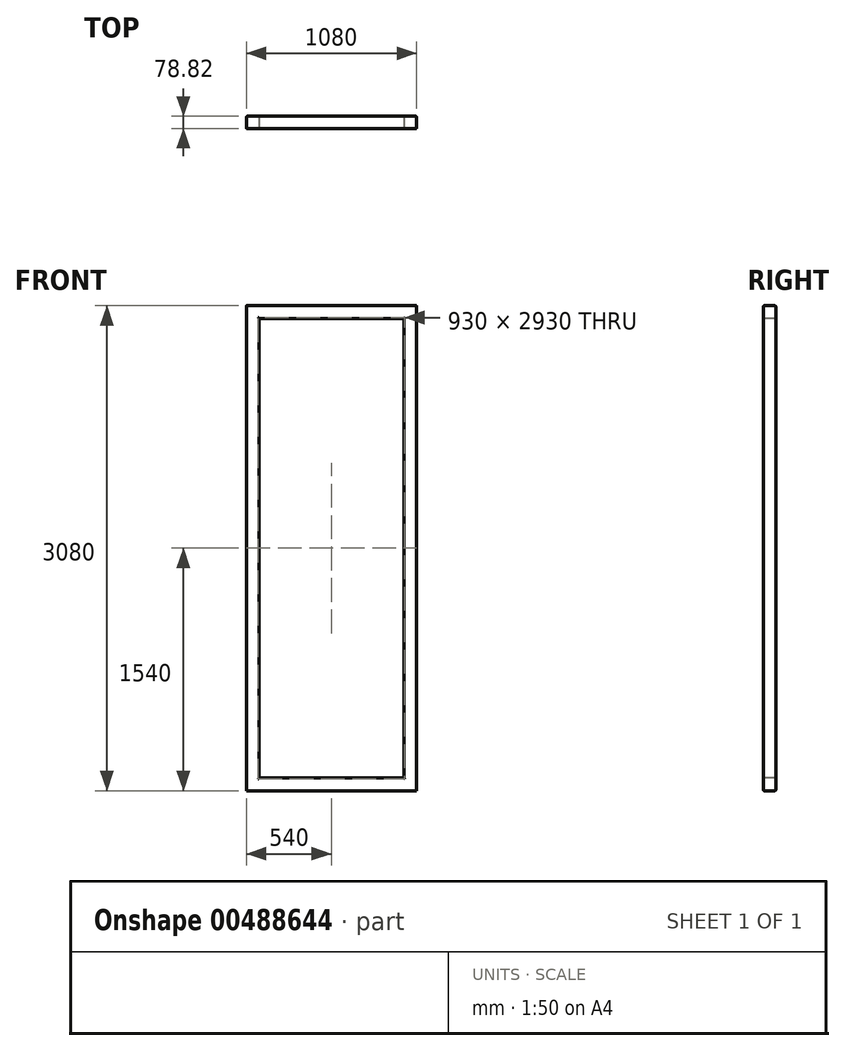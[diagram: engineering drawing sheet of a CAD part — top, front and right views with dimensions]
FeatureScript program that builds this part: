
annotation { "Feature Type Name" : "Feature", "Feature Type Description" : "" }
export const myFeature = defineFeature(function(context is Context, id is Id, definition is map)
    precondition{}
    {
        {
            var Q0;
            Q0=qCreatedBy(makeId("Top.planeOp"),FACE);
            var sketch = newSketch(context, id + "F0", { "sketchPlane" : qUnion([Q0])});
            skLineSegment(sketch, "E0.bottom", {"start": v(35, -39.4) * mm, "end": v(-35, -39.4) * mm});
            skLineSegment(sketch, "E0.top", {"start": v(35, 39.4) * mm, "end": v(-35, 39.4) * mm});
            skLineSegment(sketch, "E0.left", {"start": v(40, -34.4) * mm, "end": v(40, 34.4) * mm});
            skLineSegment(sketch, "E0.right", {"start": v(-40, -34.4) * mm, "end": v(-40, 34.4) * mm});
            skPoint(sketch, "E0.middle", {"position": v(0, 0) * mm});
            skPoint(sketch, "E1.visualSharp", {"position": v(-40, -39.4) * mm});
            skArc(sketch, "E1.filletArc", {"start": v(-40, -34.4) * mm, "mid": v(-38.54, -37.94) * mm, "end": v(-35, -39.4) * mm});
            skPoint(sketch, "E2.visualSharp", {"position": v(-40, 39.4) * mm});
            skArc(sketch, "E2.filletArc", {"start": v(-35, 39.4) * mm, "mid": v(-38.54, 37.94) * mm, "end": v(-40, 34.4) * mm});
            skPoint(sketch, "E3.visualSharp", {"position": v(40, 39.4) * mm});
            skArc(sketch, "E3.filletArc", {"start": v(40, 34.4) * mm, "mid": v(38.54, 37.94) * mm, "end": v(35, 39.4) * mm});
            skPoint(sketch, "E4.visualSharp", {"position": v(40, -39.4) * mm});
            skArc(sketch, "E4.filletArc", {"start": v(35, -39.4) * mm, "mid": v(38.54, -37.94) * mm, "end": v(40, -34.4) * mm});
            skSolve(sketch);
        }
        {
            var Q0;
            Q0=qCreatedBy(makeId("Front.planeOp"),FACE);
            var sketch = newSketch(context, id + "F1", { "sketchPlane" : qUnion([Q0])});
            skLineSegment(sketch, "E5", {"start": v(0, 0) * mm, "end": v(0, 3000) * mm});
            skLineSegment(sketch, "E6", {"start": v(0, 3000) * mm, "end": v(1000, 3000) * mm});
            skLineSegment(sketch, "E7", {"start": v(1000, 3000) * mm, "end": v(1000, 0) * mm});
            skLineSegment(sketch, "E8", {"start": v(1000, 0) * mm, "end": v(0, 0) * mm});
            skSolve(sketch);
        }
        {
            var Q0;
            Q0 = qSketchRegion(id + "F0", true);
            var Q1;
            Q1=sQuery(id+"F1.wireOp",EDGE,"E5");
            var Q2;
            Q2=sQuery(id+"F1.wireOp",EDGE,"E6");
            var Q3;
            Q3=sQuery(id+"F1.wireOp",EDGE,"E7");
            var Q4;
            Q4=sQuery(id+"F1.wireOp",EDGE,"E8");
            sweep(context, id + "F2", {"profiles" : qUnion([Q0]), "path" : qUnion([Q1, Q2, Q3, Q4])});
        }
    });
